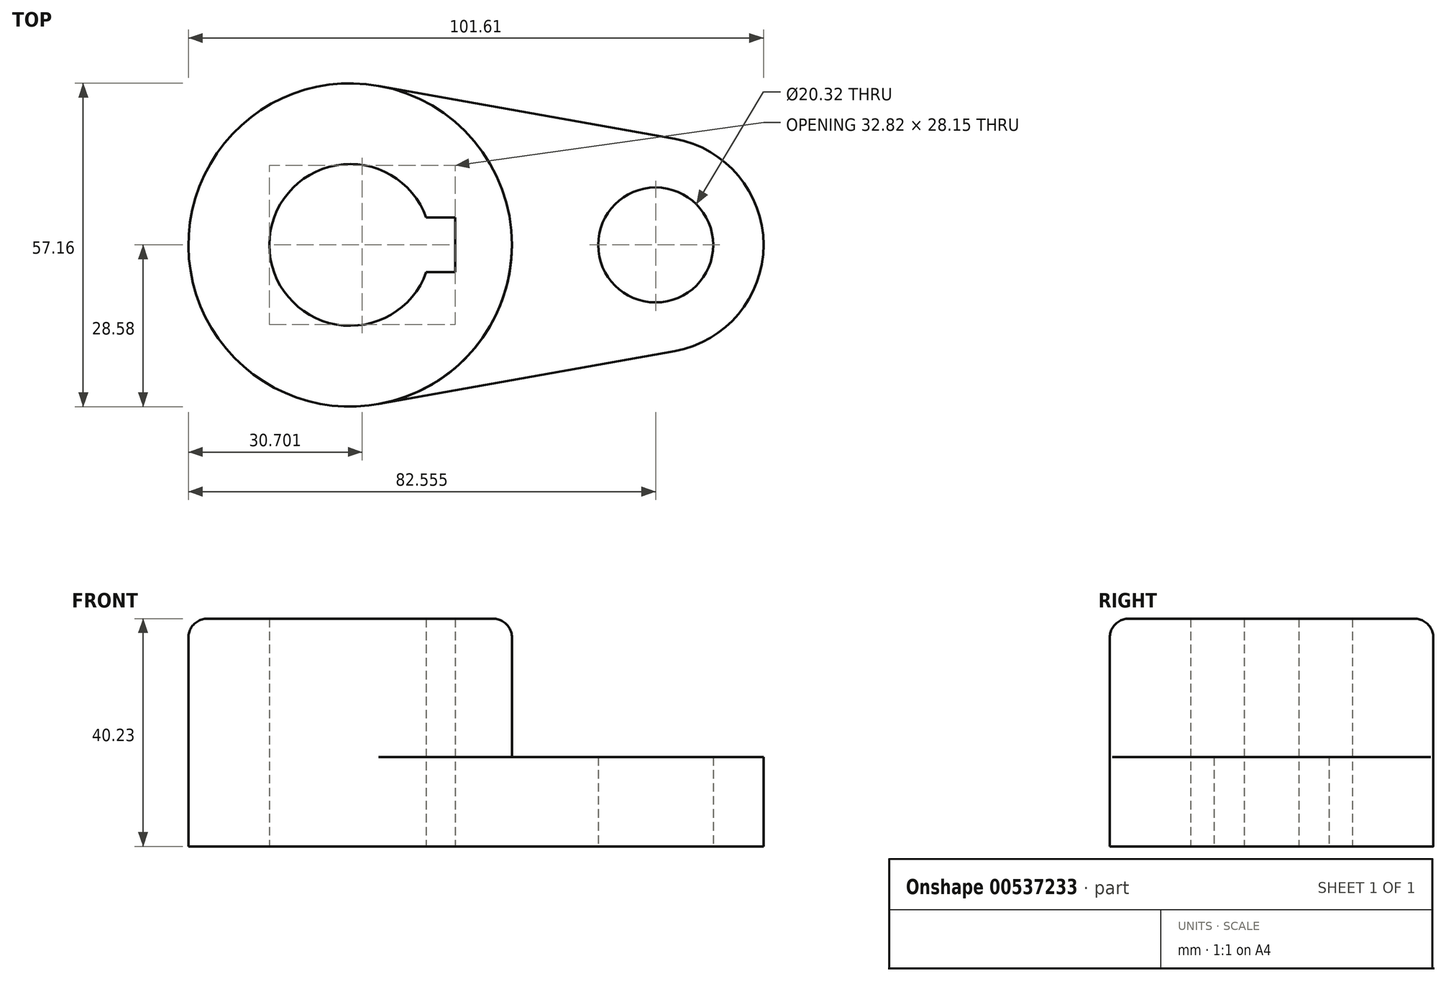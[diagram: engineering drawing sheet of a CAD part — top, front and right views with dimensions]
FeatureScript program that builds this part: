
annotation { "Feature Type Name" : "Feature", "Feature Type Description" : "" }
export const myFeature = defineFeature(function(context is Context, id is Id, definition is map)
    precondition{}
    {
        {
            var Q0;
            Q0=qCreatedBy(makeId("Top.planeOp"),FACE);
            var sketch = newSketch(context, id + "F0", { "sketchPlane" : qUnion([Q0])});
            skCircle(sketch, "E0", {"center": v(0, 0) * mm, "radius": 28.57 * mm});
            skArc(sketch, "E1", {"start": v(57.34, -18.75) * mm, "mid": v(73.03, 0) * mm, "end": v(57.34, 18.75) * mm});
            skLineSegment(sketch, "E2", {"start": v(5.04, 28.13) * mm, "end": v(57.34, 18.75) * mm});
            skLineSegment(sketch, "E3", {"start": v(5.04, -28.13) * mm, "end": v(57.34, -18.75) * mm});
            skArc(sketch, "E4", {"start": v(13.45, 4.82) * mm, "mid": v(-14.29, 0) * mm, "end": v(13.45, -4.82) * mm});
            skLineSegment(sketch, "E5", {"start": v(18.53, -4.83) * mm, "end": v(18.53, 4.82) * mm});
            skLineSegment(sketch, "E6", {"start": v(18.53, 4.82) * mm, "end": v(13.45, 4.82) * mm});
            skLineSegment(sketch, "E7.MirrorCS", {"start": v(18.53, -4.82) * mm, "end": v(13.45, -4.82) * mm});
            skCircle(sketch, "E8", {"center": v(53.98, 0) * mm, "radius": 10.16 * mm});
            skLineSegment(sketch, "E9.left", {"start": v(18.53, 4.82) * mm, "end": v(18.53, -4.82) * mm});
            skSolve(sketch);
        }
        {
            var Q0;
            Q0 = qSketchRegion(id + "F0", true);
            extrude(context, id + "F1", {"entities" : qUnion([Q0]), "depth" : 15.77 * mm, "offsetDistance" : 25.4 * mm});
        }
        {
            var Q0;
            Q0=makeQuery(id+"F1.opExtrude","CAP_FACE",FACE,{"disambiguationData":[OSD([sQuery(id+"F0.wireOp",EDGE,"E0"),sQuery(id+"F0.wireOp",EDGE,"E1"),sQuery(id+"F0.wireOp",EDGE,"E2"),sQuery(id+"F0.wireOp",EDGE,"E3"),sQuery(id+"F0.wireOp",EDGE,"E4"),sQuery(id+"F0.wireOp",EDGE,"E5"),sQuery(id+"F0.wireOp",EDGE,"E6"),sQuery(id+"F0.wireOp",EDGE,"E7.MirrorCS"),sQuery(id+"F0.wireOp",EDGE,"E8")])],"isStart":false});
            var sketch = newSketch(context, id + "F2", { "sketchPlane" : qUnion([Q0])});
            skCircle(sketch, "E10", {"center": v(0, 0) * mm, "radius": 28.58 * mm});
            skSolve(sketch);
        }
        {
            var Q0;
            Q0=makeQuery(id+"F2.imprint","IMPRINT",FACE,{"disambiguationData":[TD([[makeQuery(id+"F2.imprint","IMPRINT",EDGE,{"derivedFrom":makeQuery(id+"F1.opExtrude","CAP_EDGE",EDGE,{"disambiguationData":[OSD([sQuery(id+"F0.wireOp",EDGE,"E4")])],"isStart":false})}),-1.0]])]});
            extrude(context, id + "F3", {"entities" : qUnion([Q0]), "operationType" : NewBodyOperationType.ADD, "depth" : 24.46 * mm, "offsetDistance" : 25.4 * mm});
        }
        {
            var Q0;
            Q0=makeQuery(id+"F3.opExtrude","CAP_EDGE",EDGE,{"disambiguationData":[OSD([sQuery(id+"F2.wireOp",EDGE,"E10")])],"isStart":false});
            fillet(context, id + "F4", {"entities" : qUnion([Q0]), "radius" : 3.3 * mm, "tangentPropagation" : true, "allowEdgeOverflow" : false});
        }
    });
